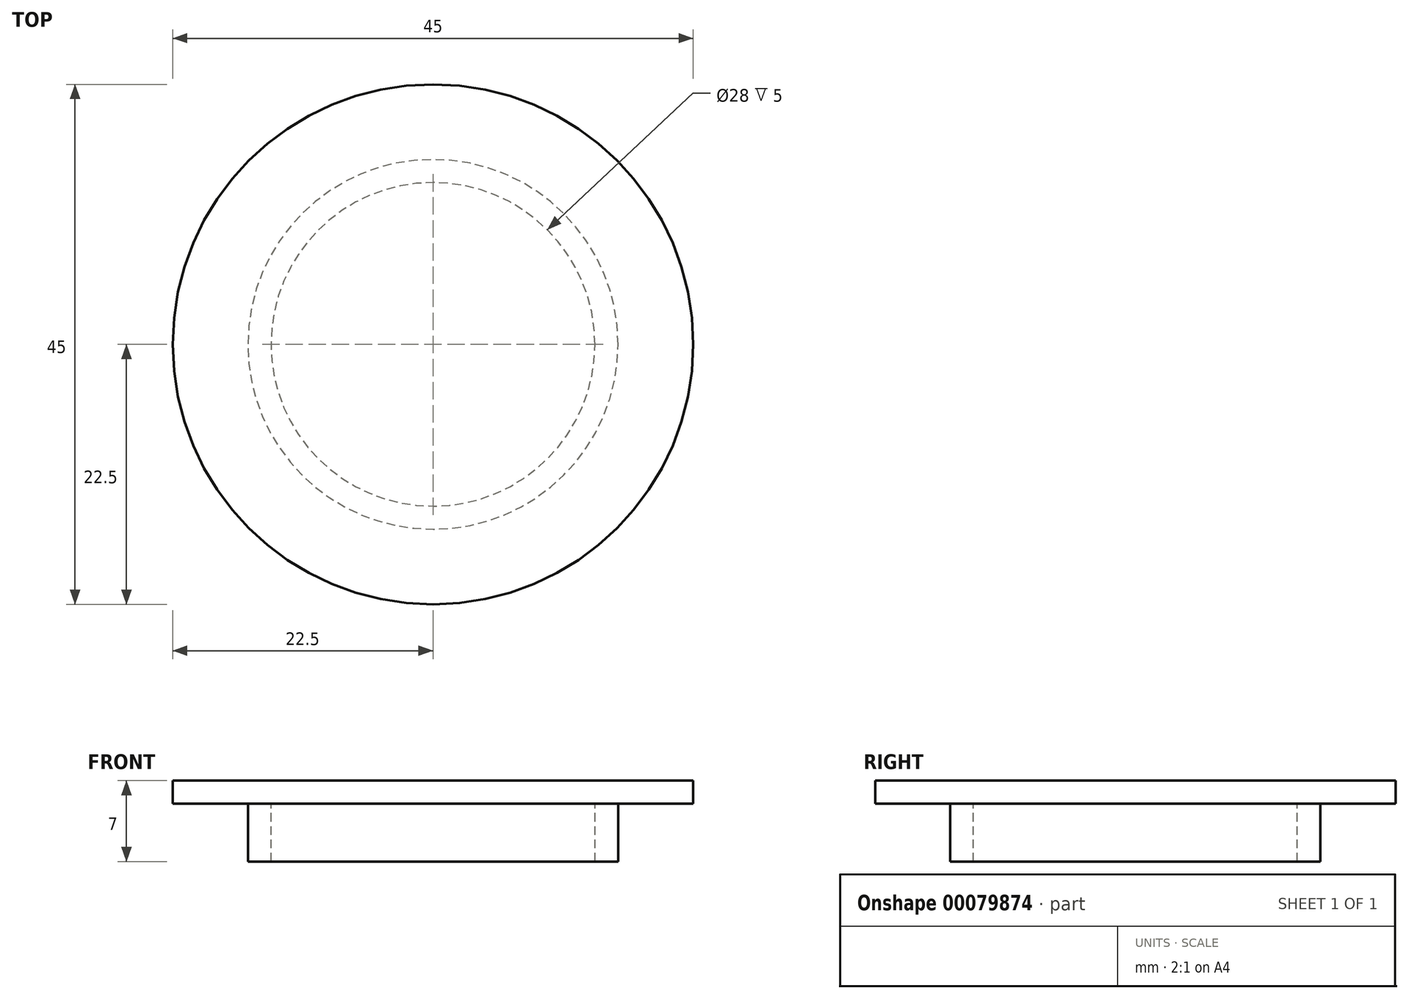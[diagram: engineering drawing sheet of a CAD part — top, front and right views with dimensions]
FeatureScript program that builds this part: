
annotation { "Feature Type Name" : "Feature", "Feature Type Description" : "" }
export const myFeature = defineFeature(function(context is Context, id is Id, definition is map)
    precondition{}
    {
        {
            var Q0;
            Q0=qCreatedBy(makeId("Top.planeOp"),FACE);
            var sketch = newSketch(context, id + "F0", { "sketchPlane" : qUnion([Q0])});
            skCircle(sketch, "E0", {"center": v(0, 0) * mm, "radius": 22.5 * mm});
            skCircle(sketch, "E1", {"center": v(0, 0) * mm, "radius": 16 * mm});
            skCircle(sketch, "E2", {"center": v(0, 0) * mm, "radius": 14 * mm});
            skSolve(sketch);
        }
        {
            var Q0;
            Q0=makeQuery(id+"F0.imprint","IMPRINT",FACE,{"disambiguationData":[TD([[makeQuery(id+"F0.imprint","IMPRINT",EDGE,{"derivedFrom":sQuery(id+"F0.wireOp",EDGE,"E2")}),1.0]])]});
            var Q1;
            Q1=makeQuery(id+"F0.imprint","IMPRINT",FACE,{"disambiguationData":[TD([[makeQuery(id+"F0.imprint","IMPRINT",EDGE,{"derivedFrom":sQuery(id+"F0.wireOp",EDGE,"E1")}),1.0]])]});
            var Q2;
            Q2=makeQuery(id+"F0.imprint","IMPRINT",FACE,{"disambiguationData":[TD([[makeQuery(id+"F0.imprint","IMPRINT",EDGE,{"derivedFrom":sQuery(id+"F0.wireOp",EDGE,"E0")}),1.0]])]});
            extrude(context, id + "F1", {"entities" : qUnion([Q0, Q1, Q2]), "depth" : 2 * mm});
        }
        {
            var Q0;
            Q0=makeQuery(id+"F0.imprint","IMPRINT",FACE,{"disambiguationData":[TD([[makeQuery(id+"F0.imprint","IMPRINT",EDGE,{"derivedFrom":sQuery(id+"F0.wireOp",EDGE,"E1")}),1.0]])]});
            extrude(context, id + "F2", {"entities" : qUnion([Q0]), "oppositeDirection" : true, "depth" : 5 * mm});
        }
    });
